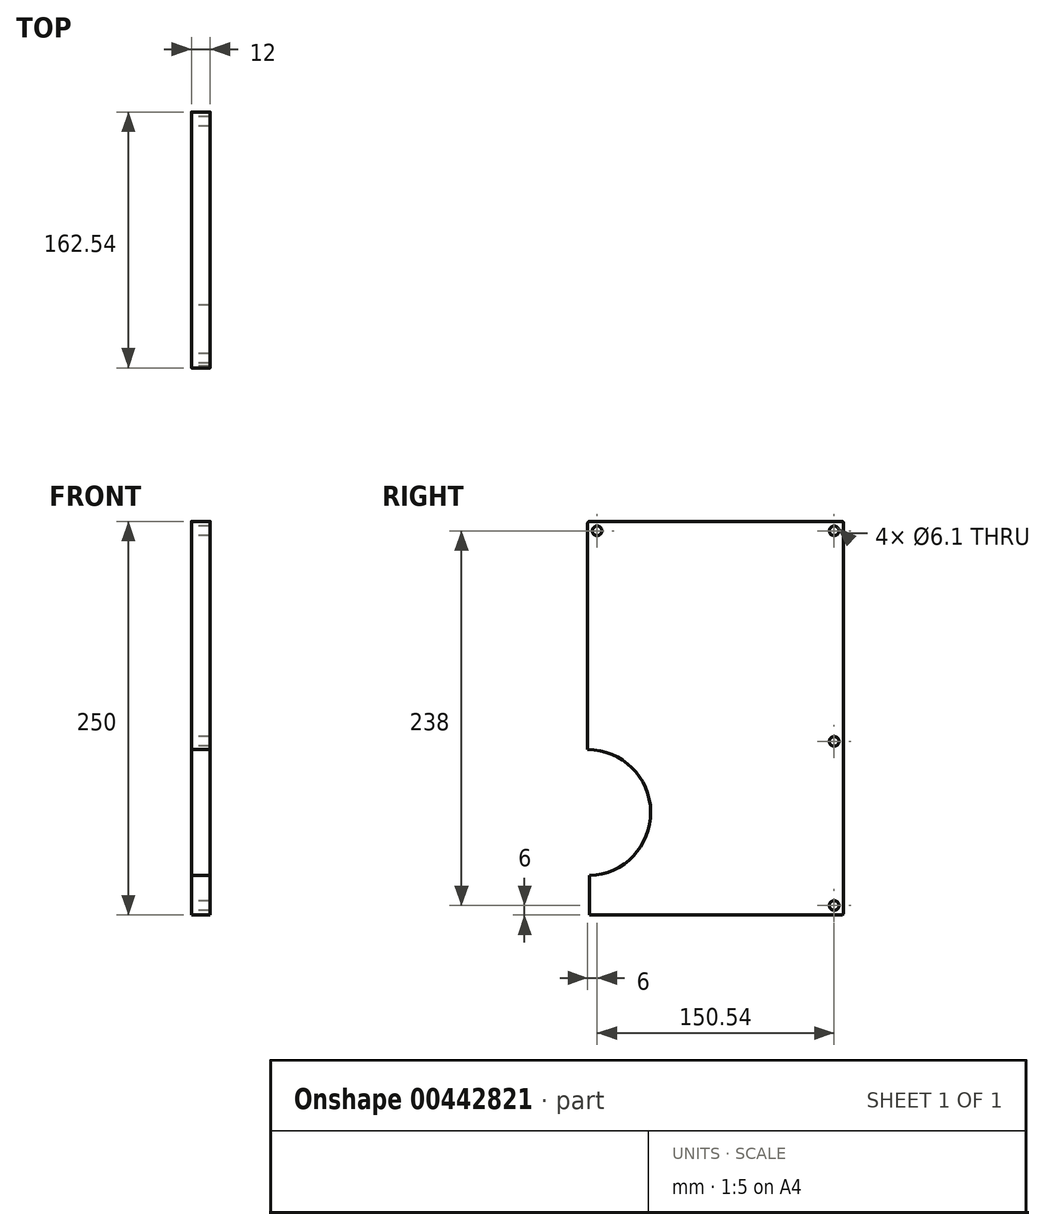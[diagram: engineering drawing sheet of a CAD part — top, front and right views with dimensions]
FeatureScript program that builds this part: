
annotation { "Feature Type Name" : "Feature", "Feature Type Description" : "" }
export const myFeature = defineFeature(function(context is Context, id is Id, definition is map)
    precondition{}
    {
        {
            var Q0;
            Q0=qCreatedBy(makeId("Right.planeOp"),FACE);
            var sketch = newSketch(context, id + "F0", { "sketchPlane" : qUnion([Q0])});
            skLineSegment(sketch, "E0.bottom", {"start": v(-1.27, 0) * mm, "end": v(-161.27, 0) * mm});
            skLineSegment(sketch, "E0.top", {"start": v(-1.27, 250) * mm, "end": v(-161.27, 250) * mm});
            skLineSegment(sketch, "E0.left", {"start": v(0, 1.27) * mm, "end": v(0, 248.73) * mm});
            skPoint(sketch, "E1.visualSharp", {"position": v(-83.54, 32.64) * mm});
            skLineSegment(sketch, "E2.trimOffspring", {"start": v(-162.54, 105) * mm, "end": v(-162.54, 248.73) * mm});
            skCircle(sketch, "E3", {"center": v(-156.54, 244) * mm, "radius": 3.05 * mm});
            skCircle(sketch, "E4", {"center": v(-6, 244) * mm, "radius": 3.05 * mm});
            skCircle(sketch, "E5", {"center": v(-6, 6) * mm, "radius": 3.05 * mm});
            skCircle(sketch, "E6", {"center": v(-6, 110.27) * mm, "radius": 3.05 * mm});
            skPoint(sketch, "E7.visualSharp", {"position": v(-162.54, 250) * mm});
            skArc(sketch, "E7.filletArc", {"start": v(-161.27, 250) * mm, "mid": v(-162.17, 249.63) * mm, "end": v(-162.54, 248.73) * mm});
            skPoint(sketch, "E8.visualSharp", {"position": v(0, 250) * mm});
            skArc(sketch, "E8.filletArc", {"start": v(0, 248.73) * mm, "mid": v(-0.37, 249.63) * mm, "end": v(-1.27, 250) * mm});
            skPoint(sketch, "E9.visualSharp", {"position": v(0, 0) * mm});
            skArc(sketch, "E9.filletArc", {"start": v(-1.27, 0) * mm, "mid": v(-0.37, 0.37) * mm, "end": v(0, 1.27) * mm});
            skLineSegment(sketch, "E10", {"start": v(-161.27, 0) * mm, "end": v(-161.27, 25) * mm});
            skArc(sketch, "E11", {"start": v(-161.27, 25) * mm, "mid": v(-122.53, 65.62) * mm, "end": v(-162.54, 105) * mm});
            skSolve(sketch);
        }
        {
            var Q0;
            Q0=qSketchRegion(id+"F0",true);
            extrude(context, id + "F1", {"entities" : qUnion([Q0]), "depth" : 12 * mm, "offsetDistance" : 25 * mm});
        }
    });
